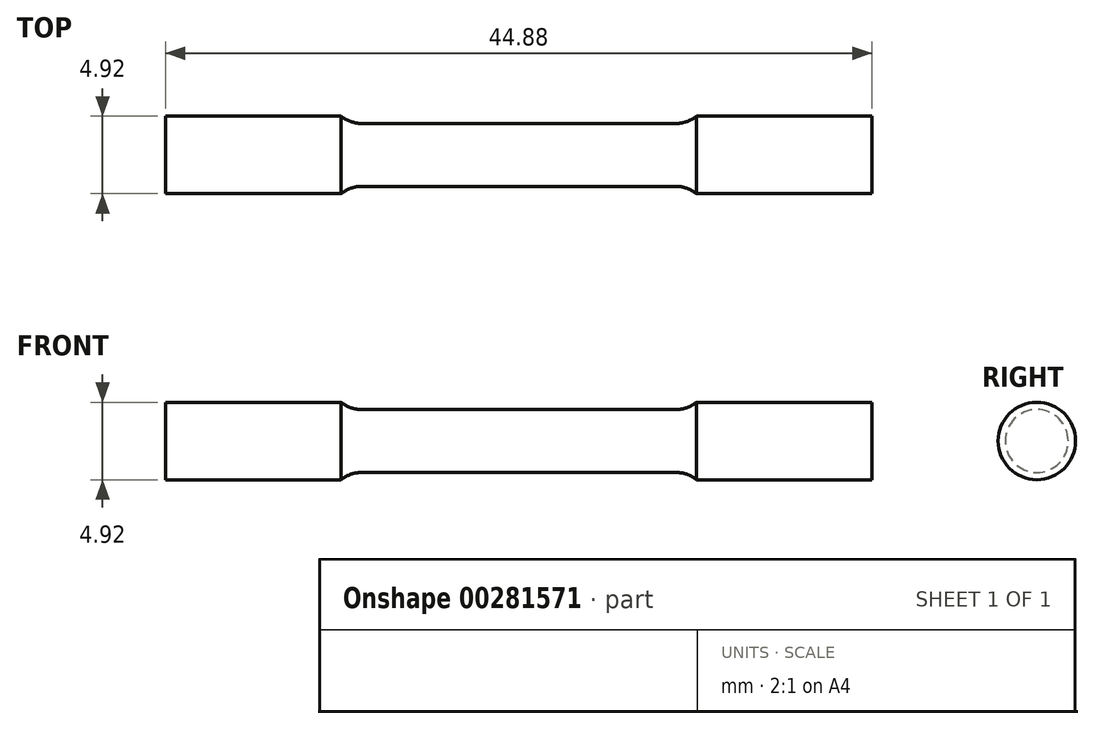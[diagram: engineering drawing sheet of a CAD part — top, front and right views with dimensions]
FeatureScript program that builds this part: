
annotation { "Feature Type Name" : "Feature", "Feature Type Description" : "" }
export const myFeature = defineFeature(function(context is Context, id is Id, definition is map)
    precondition{}
    {
        {
            var Q0;
            Q0=qCreatedBy(makeId("Front.planeOp"),FACE);
            var sketch = newSketch(context, id + "F0", { "sketchPlane" : qUnion([Q0])});
            skLineSegment(sketch, "E0", {"start": v(0, 2) * mm, "end": v(10, 2) * mm});
            skArc(sketch, "E1", {"start": v(10, 2) * mm, "mid": v(10.68, 2.12) * mm, "end": v(11.27, 2.46) * mm});
            skLineSegment(sketch, "E2", {"start": v(11.27, 2.46) * mm, "end": v(22.44, 2.46) * mm});
            skLineSegment(sketch, "E3", {"start": v(22.44, 2.46) * mm, "end": v(22.44, 0) * mm});
            skArc(sketch, "E4.MirrorCS", {"start": v(-10, 2) * mm, "mid": v(-10.68, 2.12) * mm, "end": v(-11.27, 2.46) * mm});
            skLineSegment(sketch, "E5.MirrorCS", {"start": v(-22.44, 2.46) * mm, "end": v(-22.44, 0) * mm});
            skLineSegment(sketch, "E6.MirrorCS", {"start": v(-11.27, 2.46) * mm, "end": v(-22.44, 2.46) * mm});
            skLineSegment(sketch, "E7.MirrorCS", {"start": v(0, 2) * mm, "end": v(-10, 2) * mm});
            skLineSegment(sketch, "E8", {"start": v(-22.44, 0) * mm, "end": v(22.44, 0) * mm});
            skSolve(sketch);
        }
        {
            var Q0;
            Q0 = qSketchRegion(id + "F0", true);
            var Q1;
            Q1=sQuery(id+"F0.wireOp",EDGE,"E8");
            revolve(context, id + "F1", {"entities" : qUnion([Q0]), "axis" : qUnion([Q1]), "revolveType" : RevolveType.FULL});
        }
    });
